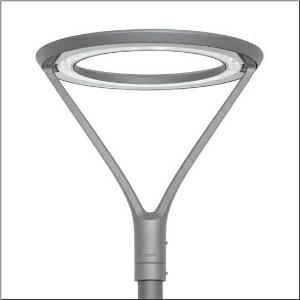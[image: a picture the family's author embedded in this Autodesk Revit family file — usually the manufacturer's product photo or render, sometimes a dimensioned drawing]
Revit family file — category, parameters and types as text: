
# Revit family: dl_r__20_led___p1_0a_5xa51283wr008_92c4
name_source: partatom
category: Lighting Fixtures
units: mm (PartAtom-declared; Revit-internal decimal feet)

## family parameters
Cut with Voids When Loaded = No
Host = Face
Light Source = No
Part Type = Normal
Room Calculation Point = No
Round Connector Dimension = Use Diameter
Shared = No

## types (1)
- --- (1 x LED 3000K / CRI = 80 (unbekannt), 3060 lm, 3000K)
    Apparent Load = 36 VA
    CIE Flux Codes = 31 71 96 100 100
    Color Rendering = 80
    Color Temperature = 3000K
    Default Elevation = 1800 mm
    Description = DL® 20 LED, mast luminaire, primary light control with cycle path optic, highly specular, primary optical cover: cover, of toughened safety glass of clear glass with excellent transmission level, light distribution: P1.0a, light emission: direct distribution, primary light characteristic: asymmetric, installation type: post-top, LED High Power LED, rated luminous flux: 3.060 lm, light colour: 830, colour temperature: 3000K, control gear: ECG Plus, control: overheat protection, power reduction, digital communication interface, constant luminous flux control, time-dependent luminous flux control, flexible luminous flux parameterisation, electronic power reduction, mains connection: 220..240V, 50/60Hz, connection cable pre-assembled, cable length: 5 m, start of lifetime: 36 W, end of lifetime: 36 W, reduction: 17 W, luminaire housing, upper part, of cast aluminium, powder-coated, Siteco® metallic grey (DB 702S), diameter: 690 mm, height: 690mm, spigot size: 76mm (post-top), luminaire housing, of cast aluminium, powder-coated, Siteco® metallic grey (DB 702S), protection rating (complete): IP66, insulation class (complete): insulation class II (safety insulation), certification: CE, ENEC, VDE, impact resistance: IK08, permissible ambient temperature for indoor applications: -25..+35°C, standard-compliant lighting for roads and squares, packaging unit: 1 piece

Light Distribution: P1.0a
    Height = 690 mm
    Lamp = 1 x LED 3000K / CRI >= 80 (unbekannt)
    Lamp Light Flux = 3060 lm
    Lamp count = 1
    Length = 690 mm
    Luminous efficacy = 86 lm/W
    Manufacturer = Siteco
    ModVariant = No
    Model = 5XA51283WR008
    Number of Poles = 1
    OnlyDefault = Yes
    Power Factor = 1
    Product Name = DL® 20 LED | P1.0a
    Product group = mast luminaire | pylon top
    ProductGroupID = 6100
    Protection Class = Protection class II
    Protection Degree = IP 66
    RLX_Detail_Level = 1
    RlxData = <blob elided: 207005 chars, md5=9b0106cc>
    Socket = socket
    Standby Power = 0 W
    System Light Flux = 3060 lm
    System Power = 36 W
    Type Comments = factory setting: luminous flux: 100 % | dim-lin: 254 | 468 mA
    Type Image = l_1006001.jpg
    URL = http://relux.com
    VarID = @adj_141313
    Voltage = 0 V
    Weight = 0.00 kg
    Width = 0 mm  [stored 0 ft]

note: [stored X ft] marks values corroborated as IEEE doubles in the binary element streams (Revit-internal decimal feet)

## geometry (parser evidence)
native form markers: Blend x4, Sweep x12
no freeform markers — native parametric forms only
